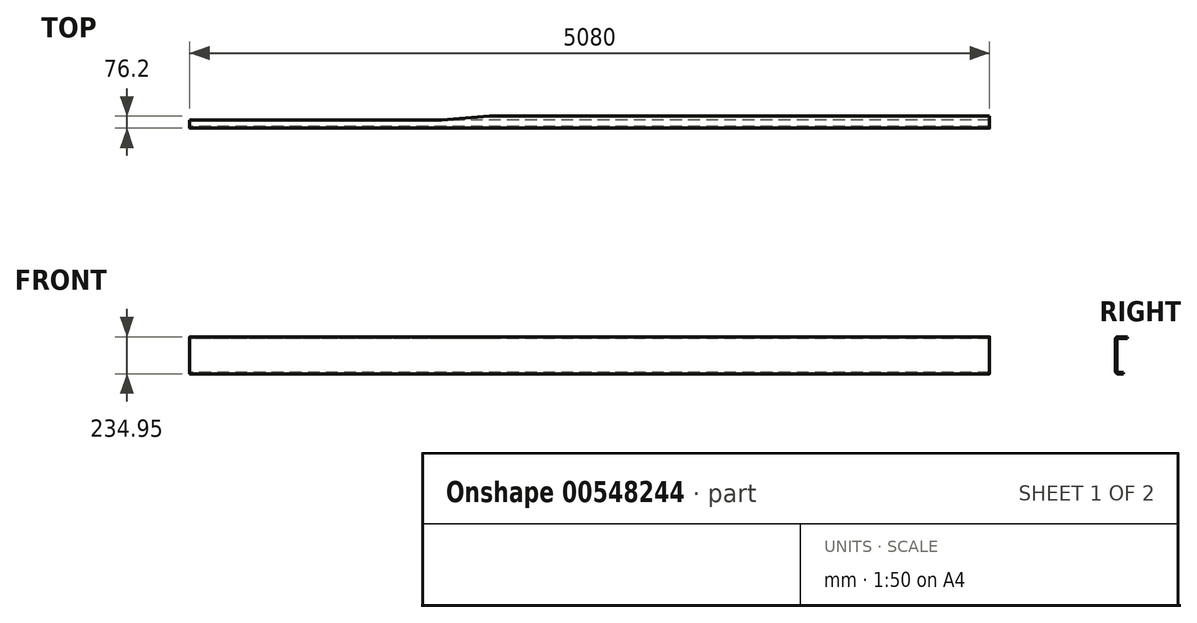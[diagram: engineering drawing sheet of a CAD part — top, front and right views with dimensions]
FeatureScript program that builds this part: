
annotation { "Feature Type Name" : "Feature", "Feature Type Description" : "" }
export const myFeature = defineFeature(function(context is Context, id is Id, definition is map)
    precondition{}
    {
        {
            var Q0;
            Q0=qCreatedBy(makeId("Right.planeOp"),FACE);
            var sketch = newSketch(context, id + "F0", { "sketchPlane" : qUnion([Q0])});
            skLineSegment(sketch, "E0", {"start": v(-431.8, 0) * mm, "end": v(-431.8, 104.78) * mm});
            skLineSegment(sketch, "E1", {"start": v(-419.1, 117.48) * mm, "end": v(-355.6, 117.48) * mm});
            skLineSegment(sketch, "E2", {"start": v(-431.8, 0) * mm, "end": v(-431.8, -104.77) * mm});
            skLineSegment(sketch, "E3", {"start": v(-419.1, -117.47) * mm, "end": v(-381, -117.47) * mm});
            skPoint(sketch, "E4.visualSharp", {"position": v(-431.8, 117.48) * mm});
            skArc(sketch, "E4.filletArc", {"start": v(-419.1, 117.48) * mm, "mid": v(-428.08, 113.76) * mm, "end": v(-431.8, 104.78) * mm});
            skPoint(sketch, "E5.visualSharp", {"position": v(-431.8, -117.47) * mm});
            skArc(sketch, "E5.filletArc", {"start": v(-431.8, -104.77) * mm, "mid": v(-428.08, -113.76) * mm, "end": v(-419.1, -117.47) * mm});
            skLineSegment(sketch, "E6.0", {"start": v(-419.1, 107.95) * mm, "end": v(-355.6, 107.95) * mm});
            skLineSegment(sketch, "E6.1", {"start": v(-422.28, 0) * mm, "end": v(-422.28, 104.78) * mm});
            skLineSegment(sketch, "E6.2", {"start": v(-422.28, 0) * mm, "end": v(-422.28, -104.77) * mm});
            skLineSegment(sketch, "E6.3", {"start": v(-419.1, -107.95) * mm, "end": v(-381, -107.95) * mm});
            skLineSegment(sketch, "E7", {"start": v(-355.6, 117.48) * mm, "end": v(-355.6, 107.95) * mm});
            skLineSegment(sketch, "E8", {"start": v(-381, -107.95) * mm, "end": v(-381, -117.47) * mm});
            skPoint(sketch, "E9.visualSharp", {"position": v(-422.28, 107.95) * mm});
            skArc(sketch, "E9.filletArc", {"start": v(-419.1, 107.95) * mm, "mid": v(-421.35, 107.02) * mm, "end": v(-422.28, 104.78) * mm});
            skPoint(sketch, "E10.visualSharp", {"position": v(-422.28, -107.95) * mm});
            skArc(sketch, "E10.filletArc", {"start": v(-422.28, -104.77) * mm, "mid": v(-421.35, -107.02) * mm, "end": v(-419.1, -107.95) * mm});
            skSolve(sketch);
        }
        {
            var Q0;
            Q0=makeQuery(id+"F0.imprint","IMPRINT",FACE,{"disambiguationData":[TD([[makeQuery(id+"F0.imprint","IMPRINT",EDGE,{"derivedFrom":sQuery(id+"F0.wireOp",EDGE,"E0")}),-1.0]])]});
            extrude(context, id + "F1", {"entities" : qUnion([Q0]), "depth" : 5080 * mm, "offsetDistance" : 25.4 * mm});
        }
        {
            var Q0;
            Q0=makeQuery(id+"F1.opExtrude","SWEPT_FACE",FACE,{"disambiguationData":[OSD([sQuery(id+"F0.wireOp",EDGE,"E1")])]});
            var sketch = newSketch(context, id + "F2", { "sketchPlane" : qUnion([Q0])});
            skLineSegment(sketch, "E11.0", {"start": v(1905, -355.6) * mm, "end": v(0, -355.6) * mm});
            skLineSegment(sketch, "E12", {"start": v(1905, -355.6) * mm, "end": v(1600.2, -381) * mm});
            skLineSegment(sketch, "E13", {"start": v(1600.2, -381) * mm, "end": v(0, -381) * mm});
            skPoint(sketch, "E14.orphan", {"position": v(5080, -355.6) * mm});
            skLineSegment(sketch, "E15.0", {"start": v(0, -381) * mm, "end": v(0, -355.6) * mm});
            skPoint(sketch, "E16.orphan", {"position": v(0, -419.1) * mm});
            skSolve(sketch);
        }
        {
            var Q0;
            Q0 = qSketchRegion(id + "F2", true);
            extrude(context, id + "F3", {"entities" : qUnion([Q0]), "operationType" : NewBodyOperationType.REMOVE, "endBound" : BoundingType.THROUGH_ALL, "oppositeDirection" : true, "depth" : 25.4 * mm, "offsetDistance" : 25.4 * mm});
        }
    });
